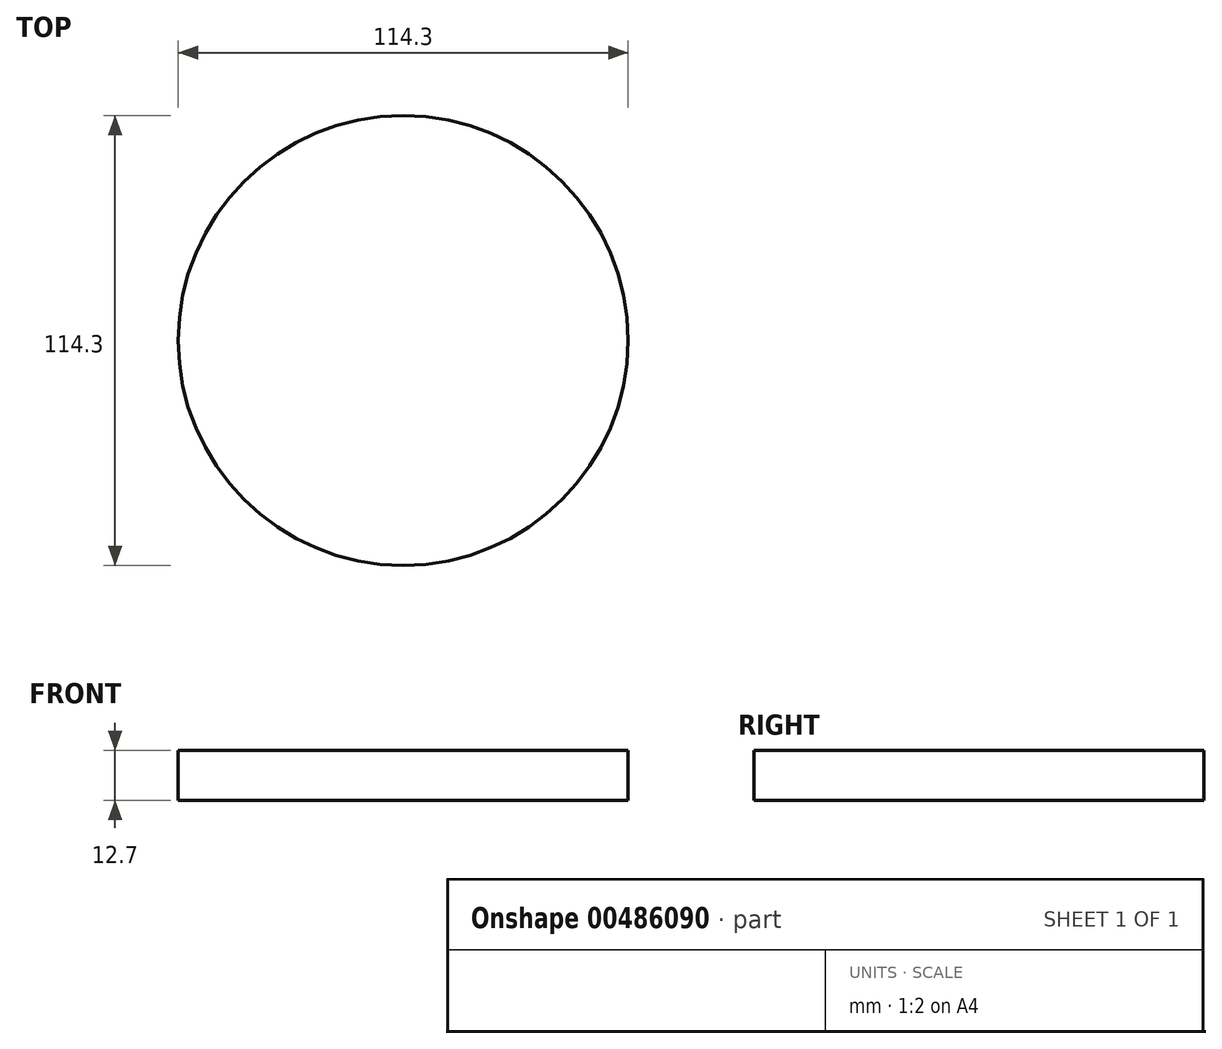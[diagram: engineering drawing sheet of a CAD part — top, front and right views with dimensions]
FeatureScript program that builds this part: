
annotation { "Feature Type Name" : "Feature", "Feature Type Description" : "" }
export const myFeature = defineFeature(function(context is Context, id is Id, definition is map)
    precondition{}
    {
        {
            var Q0;
            Q0=qCreatedBy(makeId("Top.planeOp"),FACE);
            var sketch = newSketch(context, id + "F0", { "sketchPlane" : qUnion([Q0])});
            skCircle(sketch, "E0", {"center": v(0, 0) * mm, "radius": 57.15 * mm});
            skSolve(sketch);
        }
        {
            var Q0;
            Q0 = qSketchRegion(id + "F0", true);
            extrude(context, id + "F1", {"entities" : qUnion([Q0]), "depth" : 12.7 * mm});
        }
    });
